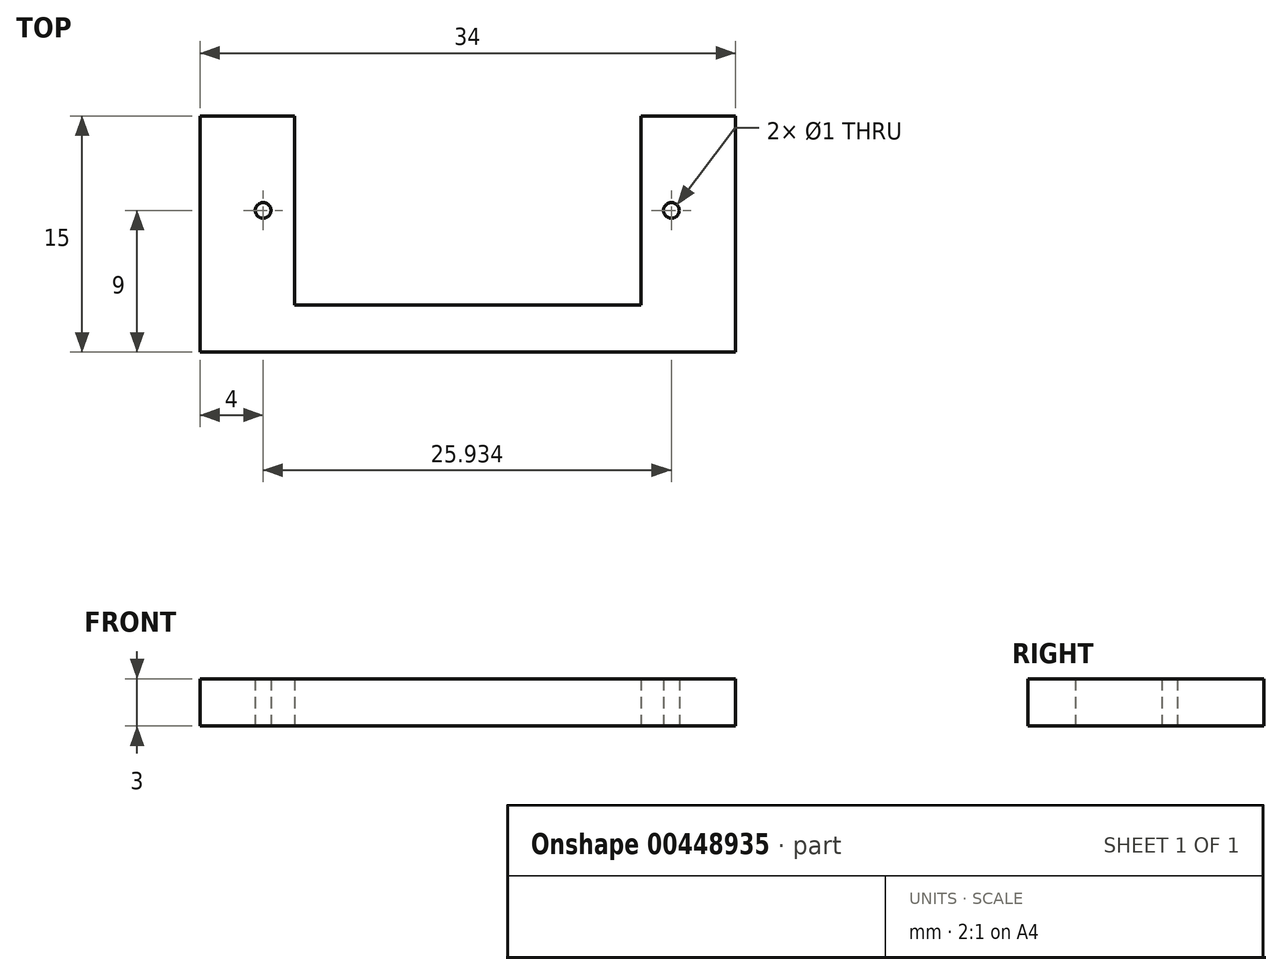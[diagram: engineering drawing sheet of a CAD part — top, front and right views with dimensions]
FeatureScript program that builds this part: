
annotation { "Feature Type Name" : "Feature", "Feature Type Description" : "" }
export const myFeature = defineFeature(function(context is Context, id is Id, definition is map)
    precondition{}
    {
        {
            var Q0;
            Q0=qCreatedBy(makeId("Top.planeOp"),FACE);
            var sketch = newSketch(context, id + "F0", { "sketchPlane" : qUnion([Q0])});
            skLineSegment(sketch, "E0", {"start": v(0, 0) * mm, "end": v(0, -15) * mm});
            skLineSegment(sketch, "E1", {"start": v(0, -15) * mm, "end": v(34, -15) * mm});
            skLineSegment(sketch, "E2", {"start": v(34, -15) * mm, "end": v(34, 0) * mm});
            skLineSegment(sketch, "E3", {"start": v(34, 0) * mm, "end": v(28, 0) * mm});
            skLineSegment(sketch, "E4", {"start": v(28, 0) * mm, "end": v(28, -12) * mm});
            skLineSegment(sketch, "E5", {"start": v(0, 0) * mm, "end": v(6, 0) * mm});
            skLineSegment(sketch, "E6", {"start": v(6, 0) * mm, "end": v(6, -12) * mm});
            skLineSegment(sketch, "E7", {"start": v(6, -12) * mm, "end": v(28, -12) * mm});
            skSolve(sketch);
        }
        {
            var Q0;
            Q0 = qSketchRegion(id + "F0", true);
            extrude(context, id + "F1", {"entities" : qUnion([Q0]), "depth" : 3 * mm});
        }
        {
            var Q0;
            Q0=qCreatedBy(makeId("Top.planeOp"),FACE);
            var sketch = newSketch(context, id + "F2", { "sketchPlane" : qUnion([Q0])});
            skLineSegment(sketch, "E8", {"start": v(0, 0) * mm, "end": v(0, -6) * mm});
            skLineSegment(sketch, "E9", {"start": v(0, -6) * mm, "end": v(4, -6) * mm});
            skSolve(sketch);
        }
        {
            var Q0;
            Q0=sQuery(id+"F2.wireOp",VERTEX,"E9.end");
            var Q1;
            Q1=makeQuery(id+"F1.opExtrude","SWEPT_BODY",BODY,{"disambiguationData":[OSD([sQuery(id+"F0.wireOp",EDGE,"E0"),sQuery(id+"F0.wireOp",EDGE,"E1"),sQuery(id+"F0.wireOp",EDGE,"E2"),sQuery(id+"F0.wireOp",EDGE,"E3"),sQuery(id+"F0.wireOp",EDGE,"E4"),sQuery(id+"F0.wireOp",EDGE,"E5"),sQuery(id+"F0.wireOp",EDGE,"E6"),sQuery(id+"F0.wireOp",EDGE,"E7")])]});
            hole(context, id + "F3", {"style" : HoleStyle.SIMPLE, "endStyle" : HoleEndStyle.THROUGH, "oppositeDirection" : true, "holeDiameter" : 1 * mm, "isTappedThrough" : true, "tappedDepth" : 12 * mm, "tapClearance" : 3, "locations" : qUnion([Q0]), "scope" : qUnion([Q1])});
        }
        {
            var Q0;
            Q0=qCreatedBy(makeId("Top.planeOp"),FACE);
            var sketch = newSketch(context, id + "F4", { "sketchPlane" : qUnion([Q0])});
            skLineSegment(sketch, "E10", {"start": v(33.54, 0) * mm, "end": v(33.54, -6) * mm});
            skLineSegment(sketch, "E11", {"start": v(33.93, -6) * mm, "end": v(29.93, -6) * mm});
            skSolve(sketch);
        }
        {
            var Q0;
            Q0=sQuery(id+"F4.wireOp",VERTEX,"E11.end");
            var Q1;
            Q1=makeQuery(id+"F1.opExtrude","SWEPT_BODY",BODY,{"disambiguationData":[OSD([sQuery(id+"F0.wireOp",EDGE,"E0"),sQuery(id+"F0.wireOp",EDGE,"E1"),sQuery(id+"F0.wireOp",EDGE,"E2"),sQuery(id+"F0.wireOp",EDGE,"E3"),sQuery(id+"F0.wireOp",EDGE,"E4"),sQuery(id+"F0.wireOp",EDGE,"E5"),sQuery(id+"F0.wireOp",EDGE,"E6"),sQuery(id+"F0.wireOp",EDGE,"E7")])]});
            hole(context, id + "F5", {"style" : HoleStyle.SIMPLE, "endStyle" : HoleEndStyle.THROUGH, "oppositeDirection" : true, "holeDiameter" : 1 * mm, "isTappedThrough" : true, "tappedDepth" : 12 * mm, "tapClearance" : 3, "locations" : qUnion([Q0]), "scope" : qUnion([Q1])});
        }
    });
